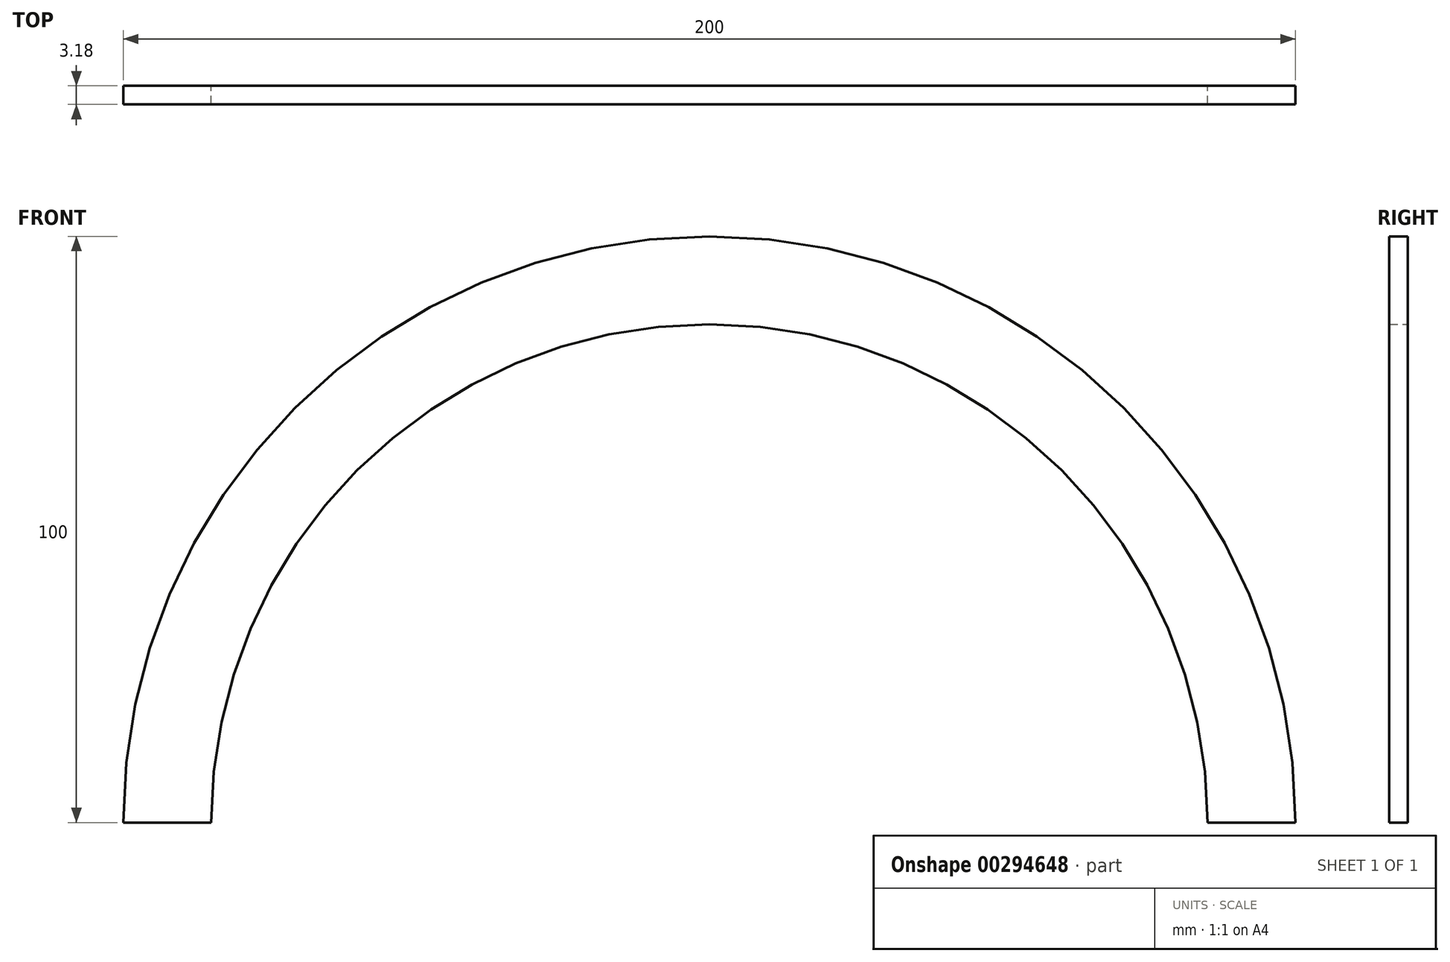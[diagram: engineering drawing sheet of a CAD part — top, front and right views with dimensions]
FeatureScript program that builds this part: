
annotation { "Feature Type Name" : "Feature", "Feature Type Description" : "" }
export const myFeature = defineFeature(function(context is Context, id is Id, definition is map)
    precondition{}
    {
        {
            var Q0;
            Q0=qCreatedBy(makeId("Front.planeOp"),FACE);
            var sketch = newSketch(context, id + "F0", { "sketchPlane" : qUnion([Q0])});
            skArc(sketch, "E0", {"start": v(100, 0) * mm, "mid": v(0, 100) * mm, "end": v(-100, 0) * mm});
            skArc(sketch, "E1", {"start": v(85, 0) * mm, "mid": v(0, 85) * mm, "end": v(-85, 0) * mm});
            skLineSegment(sketch, "E2", {"start": v(-100, 0) * mm, "end": v(-85, 0) * mm});
            skLineSegment(sketch, "E3.trimOffspring", {"start": v(85, 0) * mm, "end": v(100, 0) * mm});
            skSolve(sketch);
        }
        {
            var Q0;
            Q0 = qSketchRegion(id + "F0", true);
            extrude(context, id + "F1", {"entities" : qUnion([Q0]), "endBound" : BoundingType.SYMMETRIC, "depth" : 3.17 * mm});
        }
    });
